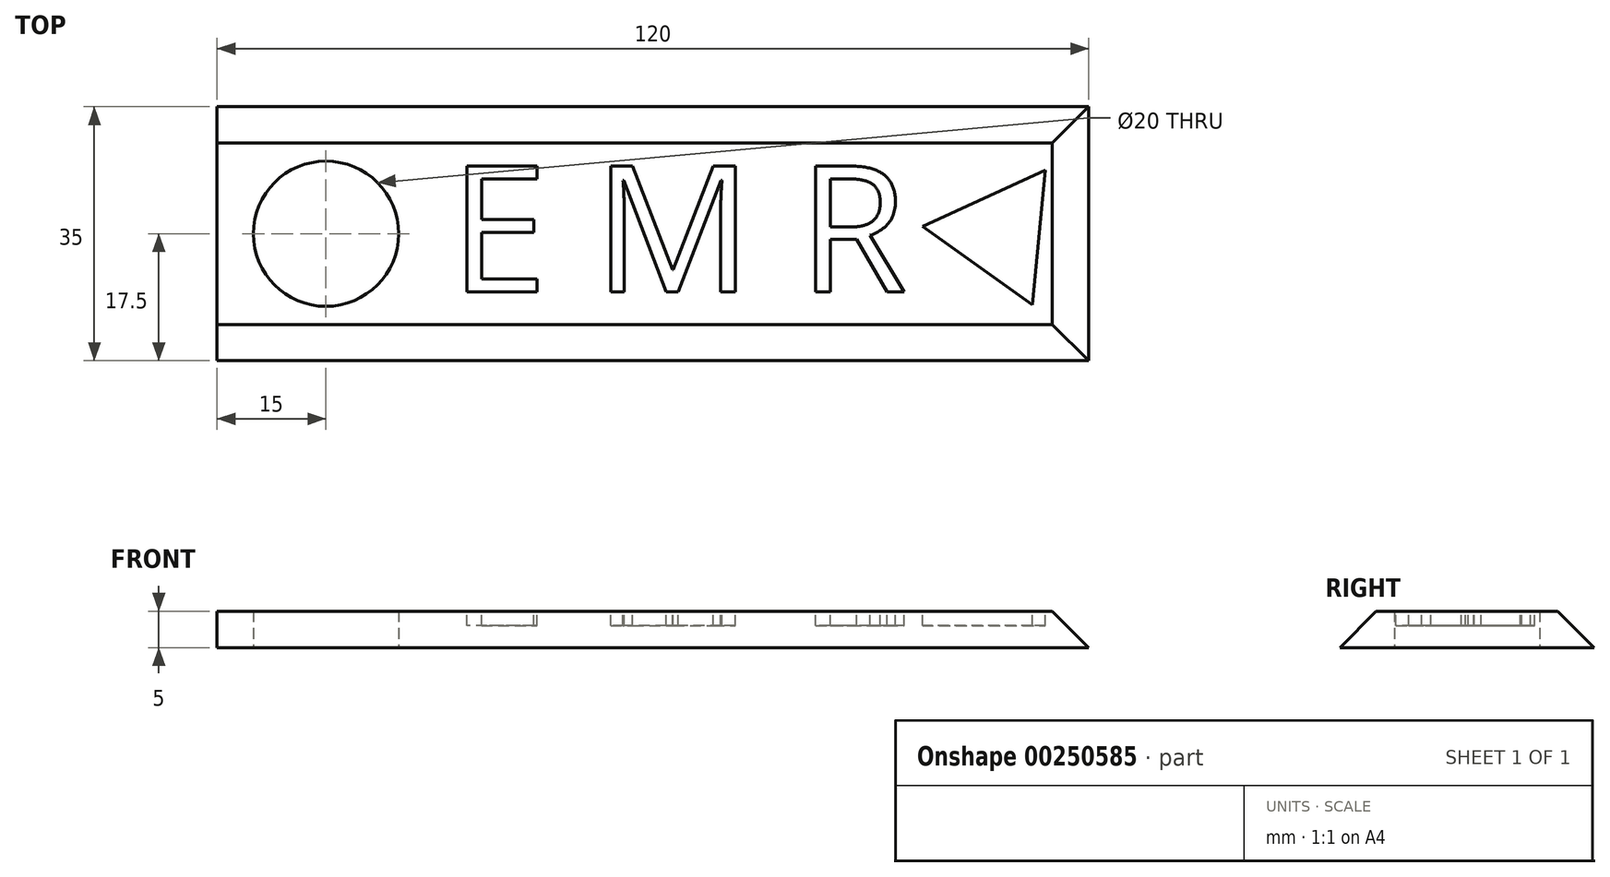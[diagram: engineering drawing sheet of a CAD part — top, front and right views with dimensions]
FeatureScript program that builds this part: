
annotation { "Feature Type Name" : "Feature", "Feature Type Description" : "" }
export const myFeature = defineFeature(function(context is Context, id is Id, definition is map)
    precondition{}
    {
        {
            var Q0;
            Q0=qCreatedBy(makeId("Top.planeOp"),FACE);
            var sketch = newSketch(context, id + "F0", { "sketchPlane" : qUnion([Q0])});
            skLineSegment(sketch, "E0.bottom", {"start": v(60, -17.5) * mm, "end": v(-60, -17.5) * mm});
            skLineSegment(sketch, "E0.top", {"start": v(60, 17.5) * mm, "end": v(-60, 17.5) * mm});
            skLineSegment(sketch, "E0.left", {"start": v(60, -17.5) * mm, "end": v(60, 17.5) * mm});
            skLineSegment(sketch, "E0.right", {"start": v(-60, -17.5) * mm, "end": v(-60, 17.5) * mm});
            skPoint(sketch, "E0.middle", {"position": v(0, 0) * mm});
            skCircle(sketch, "E1", {"center": v(-45, 0) * mm, "radius": 10 * mm});
            skSolve(sketch);
        }
        {
            var Q0;
            Q0=makeQuery(id+"F0.imprint","IMPRINT",FACE,{"disambiguationData":[TD([[makeQuery(id+"F0.imprint","IMPRINT",EDGE,{"derivedFrom":sQuery(id+"F0.wireOp",EDGE,"E0.bottom")}),-1.0]])]});
            extrude(context, id + "F1", {"entities" : qUnion([Q0]), "depth" : 5 * mm});
        }
        {
            var Q0;
            Q0=makeQuery(id+"F1.opExtrude","CAP_FACE",FACE,{"disambiguationData":[OSD([sQuery(id+"F0.wireOp",EDGE,"E0.bottom"),sQuery(id+"F0.wireOp",EDGE,"E0.top"),sQuery(id+"F0.wireOp",EDGE,"E0.left"),sQuery(id+"F0.wireOp",EDGE,"E0.right"),sQuery(id+"F0.wireOp",EDGE,"E1")])],"isStart":false});
            var sketch = newSketch(context, id + "F2", { "sketchPlane" : qUnion([Q0])});
            skText(sketch, "E2", { "text": "E M R", "fontName": "OpenSans-Regular.ttf"});
            skCircle(sketch, "E3.cCircle", {"center": v(47.81, 0) * mm, "radius": 10.73 * mm, "construction": true});
            skLineSegment(sketch, "E3.0", {"start": v(52.25, -9.77) * mm, "end": v(37.13, 1.04) * mm});
            skLineSegment(sketch, "E3.1", {"start": v(37.13, 1.04) * mm, "end": v(54.05, 8.73) * mm});
            skLineSegment(sketch, "E3.2", {"start": v(54.05, 8.73) * mm, "end": v(52.25, -9.77) * mm});
            const initialGuessF2  = {"E2": [-0.02798, -0.008, 1, 0, 0.01747]};
            skSetInitialGuess(sketch, initialGuessF2);
            skSolve(sketch);
        }
        {
            var Q0;
            Q0 = qSketchRegion(id + "F2", true);
            extrude(context, id + "F3", {"entities" : qUnion([Q0]), "operationType" : NewBodyOperationType.REMOVE, "oppositeDirection" : true, "depth" : 2 * mm});
        }
        {
            var Q0;
            Q0=makeQuery(id+"F1.opExtrude","CAP_EDGE",EDGE,{"disambiguationData":[OSD([sQuery(id+"F0.wireOp",EDGE,"E0.bottom")])],"isStart":false});
            var Q1;
            Q1=makeQuery(id+"F1.opExtrude","CAP_EDGE",EDGE,{"disambiguationData":[OSD([sQuery(id+"F0.wireOp",EDGE,"E0.left")])],"isStart":false});
            var Q2;
            Q2=makeQuery(id+"F1.opExtrude","CAP_EDGE",EDGE,{"disambiguationData":[OSD([sQuery(id+"F0.wireOp",EDGE,"E0.top")])],"isStart":false});
            chamfer(context, id + "F4", {"entities" : qUnion([Q0, Q1, Q2]), "width" : 5 * mm, "tangentPropagation" : true});
        }
    });
